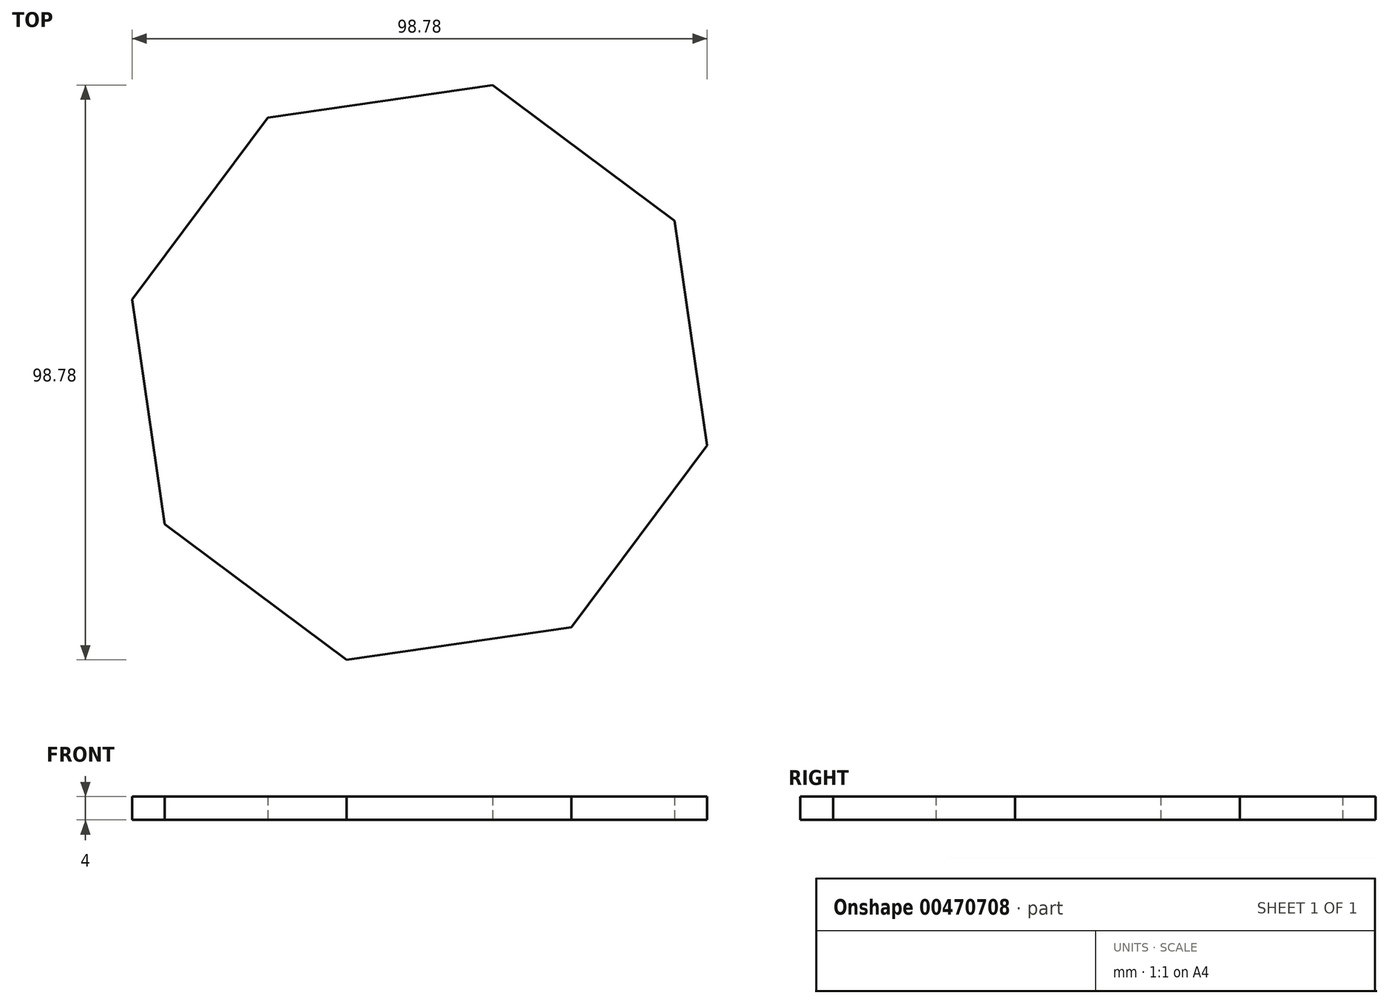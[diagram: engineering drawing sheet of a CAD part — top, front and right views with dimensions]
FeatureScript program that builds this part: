
annotation { "Feature Type Name" : "Feature", "Feature Type Description" : "" }
export const myFeature = defineFeature(function(context is Context, id is Id, definition is map)
    precondition{}
    {
        {
            var Q0;
            Q0=qCreatedBy(makeId("Top.planeOp"),FACE);
            var sketch = newSketch(context, id + "F0", { "sketchPlane" : qUnion([Q0])});
            skCircle(sketch, "E0.cCircle", {"center": v(0, 0) * mm, "radius": 50.96 * mm, "construction": true});
            skLineSegment(sketch, "E0.0", {"start": v(26.07, -43.78) * mm, "end": v(-12.53, -49.4) * mm});
            skLineSegment(sketch, "E0.1", {"start": v(-12.53, -49.4) * mm, "end": v(-43.78, -26.07) * mm});
            skLineSegment(sketch, "E0.2", {"start": v(-43.78, -26.07) * mm, "end": v(-49.4, 12.53) * mm});
            skLineSegment(sketch, "E0.3", {"start": v(-49.4, 12.53) * mm, "end": v(-26.07, 43.78) * mm});
            skLineSegment(sketch, "E0.4", {"start": v(-26.07, 43.78) * mm, "end": v(12.53, 49.4) * mm});
            skLineSegment(sketch, "E0.5", {"start": v(12.53, 49.4) * mm, "end": v(43.78, 26.07) * mm});
            skLineSegment(sketch, "E0.6", {"start": v(43.78, 26.07) * mm, "end": v(49.4, -12.53) * mm});
            skLineSegment(sketch, "E0.7", {"start": v(49.4, -12.53) * mm, "end": v(26.07, -43.78) * mm});
            skSolve(sketch);
        }
        {
            var Q0;
            Q0=makeQuery(id+"F0.imprint","IMPRINT",FACE,{"disambiguationData":[TD([[makeQuery(id+"F0.imprint","IMPRINT",EDGE,{"derivedFrom":sQuery(id+"F0.wireOp",EDGE,"E0.0")}),-1.0]])]});
            extrude(context, id + "F1", {"entities" : qUnion([Q0]), "depth" : 4 * mm});
        }
    });
